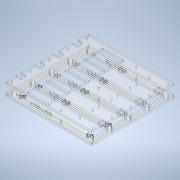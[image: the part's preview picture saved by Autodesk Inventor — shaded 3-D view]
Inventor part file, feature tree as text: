
AUTODESK INVENTOR PART (.ipt)
format: ipt  version: 2021 (Build 250183000, 183)  size: 1,787,904 bytes
history: native  units: mm
features: other x6, fillet x6, sketch x3, extrude x3, plane x3, hole x2, split x2, projected_geometry x1
ambient origin geometry x8: Origin, YZ Plane, XZ Plane, XY Plane, X Axis, Y Axis, Z Axis, Center Point
bodies: Solid1 (feature_tree), Solid3 (feature_tree)
feature tree (26):
  sketch  "Sketch1"  dims[d7=11.9mm d17=68.55mm]
  other  "Repaired Geometry1"
  extrude  "Extrusion1"  Depth=68.55mm
  extrude  "Extrusion2"  Depth=5.0mm
  hole  "Hole1"  [1 undecoded]
  hole  "Hole2"  [1 undecoded]
  plane  "Work Plane1"
  extrude  "Extrusion3"  Depth=8.0mm
  sketch  "Sketch3"  dims[d18=122.9mm d22=5.0mm]
  sketch  "Sketch4"  dims[d23=5.0mm d24=11.9mm d25=68.55mm d26=122.9mm d27=5.0mm d28=5.0mm d29=11.9mm d30=68.55mm d31=122.9mm d32=5.0mm d33=5.0mm d34=11.9mm d35=68.55mm d36=122.9mm d37=5.0mm d39=8.0mm d40=8.0mm d41=4.0mm d42=0.0mm d43=4.0mm d44=0.0mm d45=3.05mm d46=6.0mm d47=6.5mm d48=3.0mm d49=90.0deg d50=8.0mm d51=0.0mm d52=3.05mm d53=6.0mm d54=6.5mm d55=3.0mm d56=90.0deg d57=8.0mm d58=0.0mm d59=-29.0mm d60=4.0mm d61=0.0mm d62=2.75mm d63=2.75mm d66=83.0mm d67=20.7mm d68=2.75mm d76=20.0mm d77=20.0mm d79=3.0mm d80=1.0mm d81=3.0mm d82=1.0mm d87=1.0mm d88=1.0mm d90=3.0mm d91=1.0mm d92=1.0mm d93=3.0mm d94=1.0mm d95=1.0mm d97=8.0mm d98=8.0mm d99=8.0mm d100=8.0mm d101=8.0mm d102=8.0mm d103=8.0mm d104=8.0mm d105=8.0mm d106=3.5mm d107=3.5mm d108=3.5mm d109=3.5mm d110=3.5mm d111=3.5mm d112=3.5mm d113=3.5mm d114=3.5mm d115=3.5mm d116=3.5mm d117=3.5mm d118=3.5mm d119=3.5mm d120=3.5mm d121=3.5mm d122=87.371mm d149=8.5mm d150=-4.0mm d157=2.0mm d158=2.0mm d163=2.0mm d167=0.25mm d168=0.5mm d251=2.229mm d252=5.607mm d261=0.75mm d263=4.0mm d264=4.0mm d265=4.0mm d266=4.0mm d268=5.0mm d271=5.0mm d272=8.0mm d273=8.0mm d274=2.0mm d275=2.0mm d276=2.0mm d279=0.75mm d280=4.0mm d281=4.0mm d282=4.0mm d283=4.0mm d284=2.0mm d285=2.0mm d286=2.0mm d289=0.75mm d290=4.0mm d291=4.0mm d292=4.0mm d293=4.0mm d296=2.0mm d299=0.75mm d304=4.0mm d305=2.0mm d306=2.0mm d308=6.0mm d309=0.75mm d310=4.0mm d311=4.0mm d312=4.0mm d313=4.0mm d330=38.4mm d331=38.4mm d332=38.4mm d333=38.4mm d334=38.4mm d335=38.4mm d336=38.4mm d337=38.4mm d338=34.0mm d339=110.0mm d340=8.0mm d343=0.3mm d345=0.299997mm d346=0.1mm d347=0.15mm d348=0.15mm d349=0.1mm d350=0.15mm d351=0.15mm d352=0.15mm d353=0.15mm d354=0.15mm d355=0.15mm d356=0.1mm d357=36.0mm d358=90.0deg d359=14.0mm d360=14.0mm d367=3.0mm d368=3.0mm d375=4.5mm d376=4.0mm d377=4.0mm d378=4.0mm d379=4.0mm d380=14.0mm d381=14.0mm d382=3.0mm d383=3.0mm d384=14.0mm d385=14.0mm d386=3.0mm d387=3.0mm d388=14.0mm d389=14.0mm d390=3.0mm d391=3.0mm d392=0.5mm d393=0.5mm d394=0.5mm d395=0.25mm]
  plane  "Work Plane4"
  split  "Split1"
  plane  "Work Plane3"
  split  "Split3"
  fillet  "Fillet1"  Radius=4.0mm
  fillet  "Fillet2"  Radius=4.0mm
  fillet  "Fillet3"  [1 undecoded]
  fillet  "Fillet4"  Radius=4.0mm
  fillet  "Fillet5"  Radius=2.75mm
  fillet  "Fillet6"  Radius=2.75mm
  projected_geometry  "Projected Loop1"
  other  "TopPlate"
  other  "Composite1"
  other  "Srf1"
  other  "MidPlate"
  other  "BotPlate"
note: 3 required parameter values undecoded (feature->parameter linkage not recoverable at this tier; creation-order binding heuristic only, values carry confidence <= 0.55)
